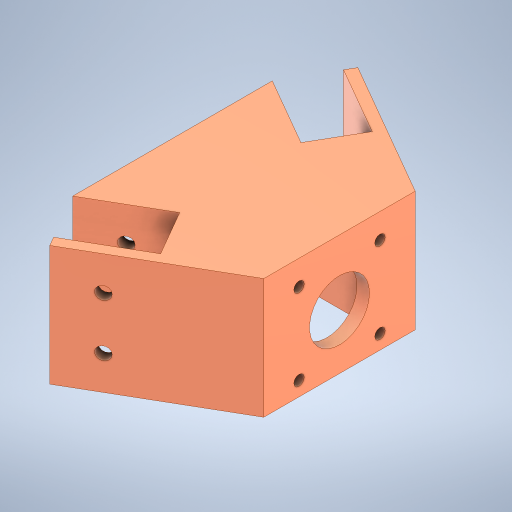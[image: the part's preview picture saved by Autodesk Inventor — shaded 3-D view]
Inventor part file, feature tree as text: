
AUTODESK INVENTOR PART (.ipt)
format: ipt  version: 2024.2 (Build 282272000, 272)  size: 341,504 bytes
history: native  units: mm
features: extrude x8, sketch x8
ambient origin geometry x8: Origin, YZ Plane, XZ Plane, XY Plane, X Axis, Y Axis, Z Axis, Center Point
bodies: Solid1 (feature_tree)
feature tree (16):
  extrude  "Extrusion1"  TaperAngle=150.0deg  [1 undecoded]
  extrude  "Extrusion2"  Depth=43.0mm
  extrude  "Extrusion3"  Depth=20.0mm
  extrude  "Extrusion4"  Depth=4.0mm
  extrude  "Extrusion5"  Depth=4.0mm TaperAngle=0.0deg
  extrude  "Extrusion6"  Depth=23.0mm
  sketch  "Sketch7"  dims[d20=31.0mm d21=31.0mm]
  extrude  "Extrusion7"  Depth=31.0mm
  extrude  "Extrusion8"  Depth=4.0mm
  sketch  "Sketch1"  dims[d1=60.0deg d3=150.0deg]
  sketch  "Sketch2"  dims[d4=43.0mm d6=55.0mm]
  sketch  "Sketch3"  dims[d8=20.0mm d9=20.0mm]
  sketch  "Sketch4"  dims[d10=4.0mm d11=4.0mm]
  sketch  "Sketch5"  dims[d14=46.0mm d15=0.0mm d16=4.0mm d17=0.0mm]
  sketch  "Sketch6"  dims[d18=21.0mm d19=23.0mm]
  sketch  "Sketch8"  dims[d22=4.0mm d23=4.0mm d24=4.0mm d25=4.0mm d29=46.0mm d30=0.0mm d32=0.0mm d33=0.0mm d34=20.0mm d35=15.0mm d36=13.0mm d37=5.0mm d38=5.0mm d39=10.0mm d40=0.0mm d41=20.0mm d42=10.0mm d43=15.0mm d44=5.0mm d45=5.0mm d46=0.0mm d47=0.0mm d48=5.0mm d49=5.0mm d50=10.0mm d51=0.0mm d52=10.0mm d53=0.0mm d54=58.0mm d55=60.0mm d56=30.0mm d57=30.0mm]
note: 1 required parameter value undecoded (feature->parameter linkage not recoverable at this tier; creation-order binding heuristic only, values carry confidence <= 0.55)
